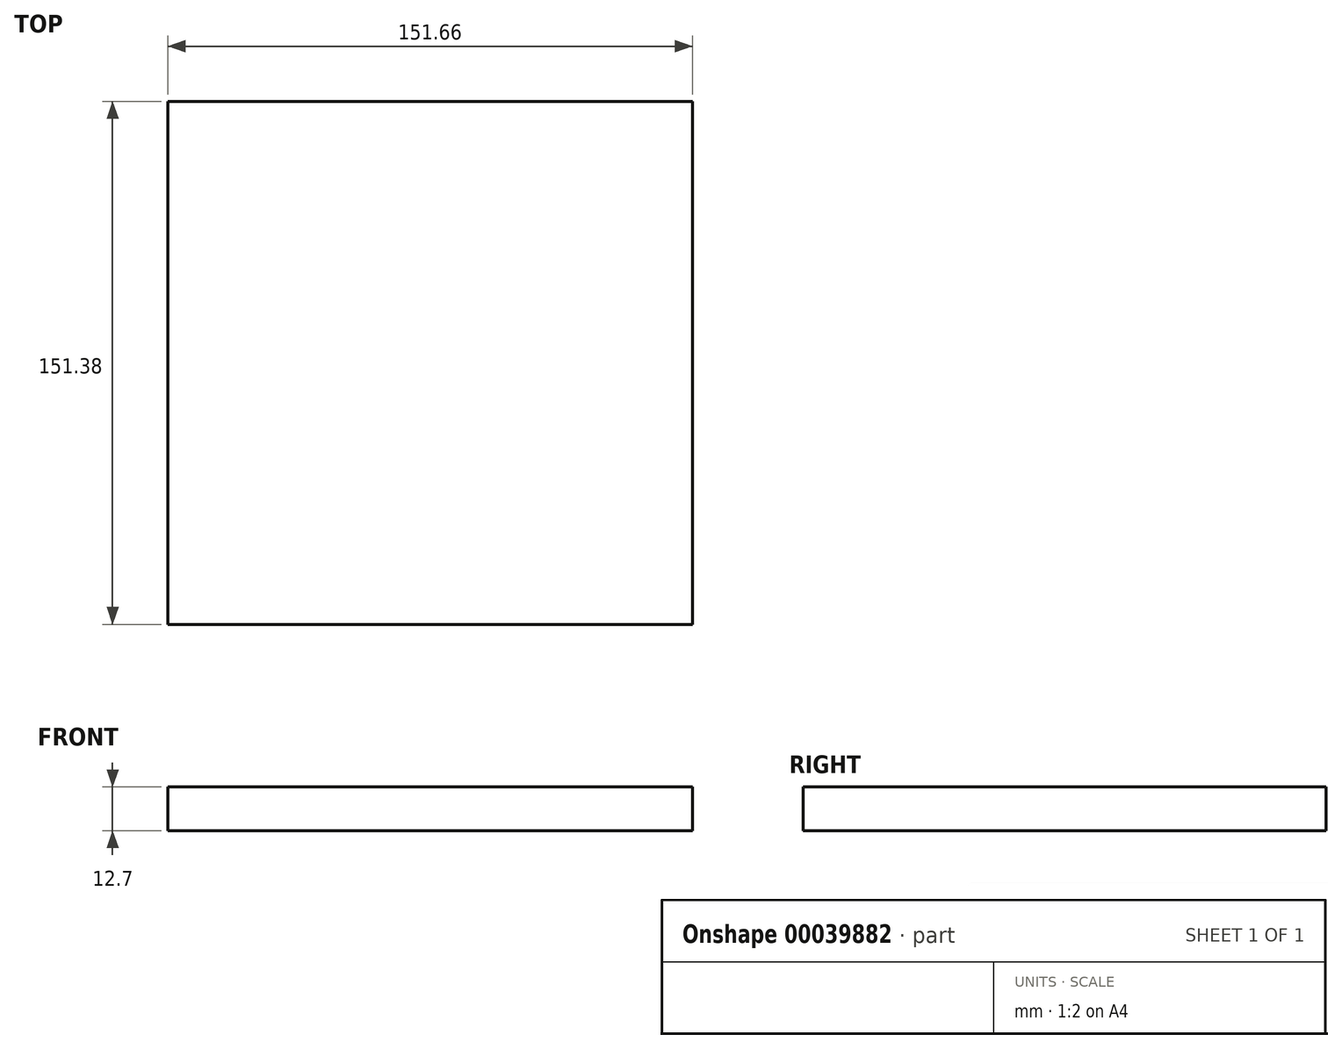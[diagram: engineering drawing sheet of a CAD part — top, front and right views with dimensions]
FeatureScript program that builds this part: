
annotation { "Feature Type Name" : "Feature", "Feature Type Description" : "" }
export const myFeature = defineFeature(function(context is Context, id is Id, definition is map)
    precondition{}
    {
        {
            var Q0;
            Q0=qCreatedBy(makeId("Top.planeOp"),FACE);
            var sketch = newSketch(context, id + "F0", { "sketchPlane" : qUnion([Q0])});
            skLineSegment(sketch, "E0.bottom", {"start": v(-75.69, -75.27) * mm, "end": v(75.97, -75.27) * mm});
            skLineSegment(sketch, "E0.top", {"start": v(-75.69, 76.1) * mm, "end": v(75.97, 76.1) * mm});
            skLineSegment(sketch, "E0.left", {"start": v(-75.69, -75.27) * mm, "end": v(-75.69, 76.1) * mm});
            skLineSegment(sketch, "E0.right", {"start": v(75.97, -75.27) * mm, "end": v(75.97, 76.1) * mm});
            skSolve(sketch);
        }
        {
            var Q0;
            Q0=makeQuery(id+"F0.imprint","IMPRINT",FACE,{"disambiguationData":[TD([[makeQuery(id+"F0.imprint","IMPRINT",EDGE,{"derivedFrom":sQuery(id+"F0.wireOp",EDGE,"E0.bottom")}),1.0]])]});
            extrude(context, id + "F1", {"entities" : qUnion([Q0]), "depth" : 12.7 * mm});
        }
    });
